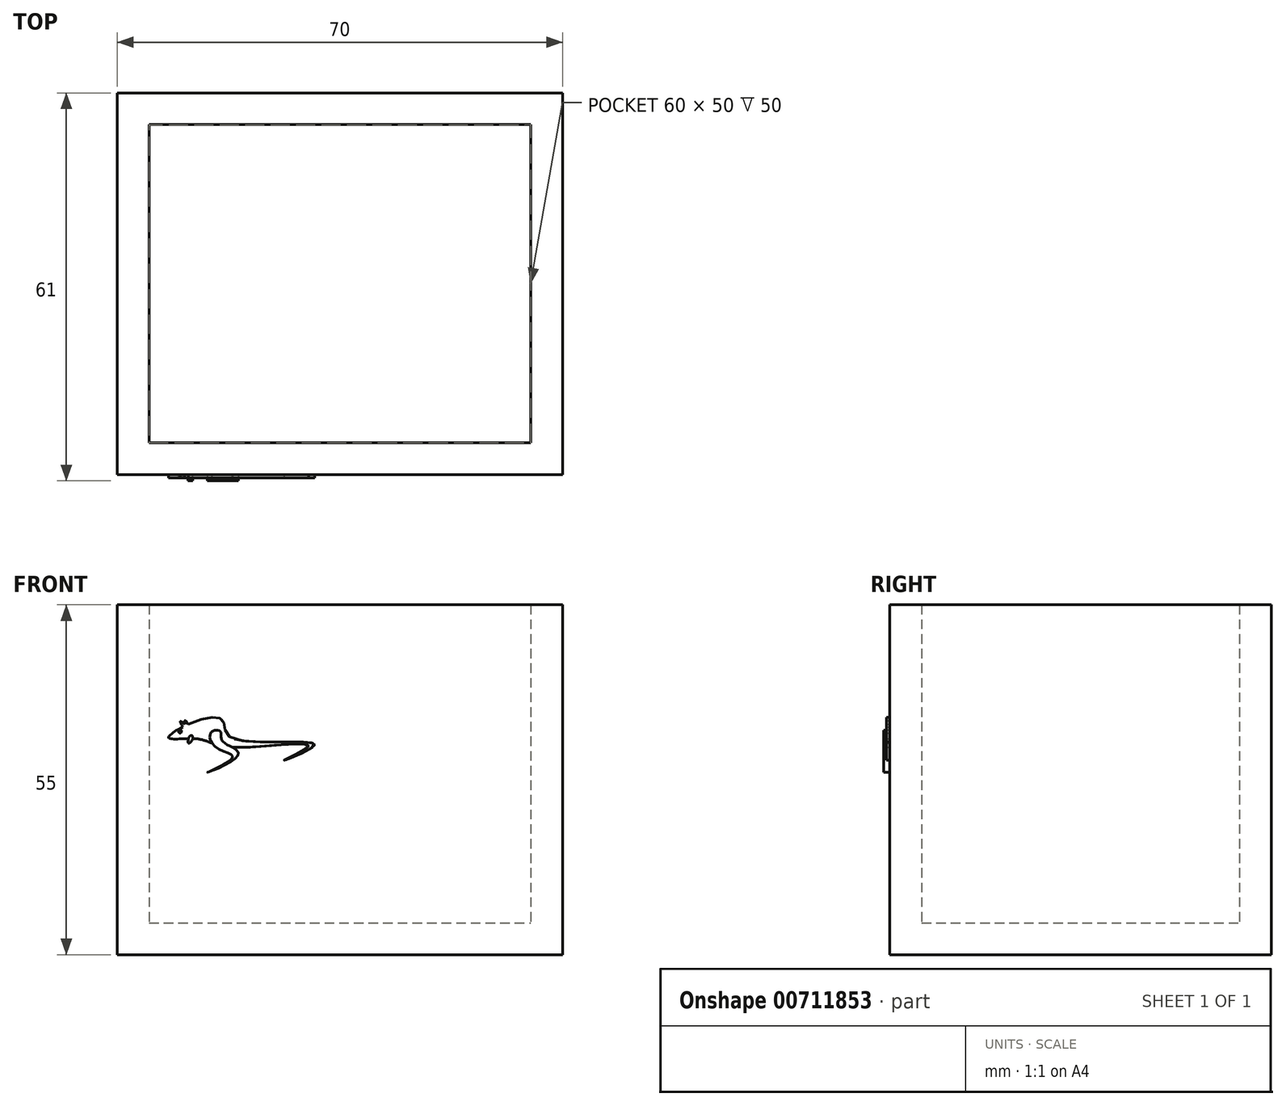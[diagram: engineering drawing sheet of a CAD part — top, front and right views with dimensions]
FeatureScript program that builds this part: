
annotation { "Feature Type Name" : "Feature", "Feature Type Description" : "" }
export const myFeature = defineFeature(function(context is Context, id is Id, definition is map)
    precondition{}
    {
        {
            var Q0;
            Q0=qCreatedBy(makeId("Top.planeOp"),FACE);
            var sketch = newSketch(context, id + "F0", { "sketchPlane" : qUnion([Q0])});
            skLineSegment(sketch, "E0.bottom", {"start": v(0, 0) * mm, "end": v(70, 0) * mm});
            skLineSegment(sketch, "E0.top", {"start": v(0, 60) * mm, "end": v(70, 60) * mm});
            skLineSegment(sketch, "E0.left", {"start": v(0, 0) * mm, "end": v(0, 60) * mm});
            skLineSegment(sketch, "E0.right", {"start": v(70, 0) * mm, "end": v(70, 60) * mm});
            skSolve(sketch);
        }
        {
            var Q0;
            Q0=makeQuery(id+"F0.imprint","IMPRINT",FACE,{"disambiguationData":[TD([[makeQuery(id+"F0.imprint","IMPRINT",EDGE,{"derivedFrom":sQuery(id+"F0.wireOp",EDGE,"E0.bottom")}),1.0]])]});
            extrude(context, id + "F1", {"entities" : qUnion([Q0]), "depth" : 5 * mm, "offsetDistance" : 25 * mm});
        }
        {
            var Q0;
            Q0=makeQuery(id+"F1.opExtrude","CAP_FACE",FACE,{"disambiguationData":[OSD([sQuery(id+"F0.wireOp",EDGE,"E0.bottom"),sQuery(id+"F0.wireOp",EDGE,"E0.top"),sQuery(id+"F0.wireOp",EDGE,"E0.left"),sQuery(id+"F0.wireOp",EDGE,"E0.right")])],"isStart":false});
            var sketch = newSketch(context, id + "F2", { "sketchPlane" : qUnion([Q0])});
            skLineSegment(sketch, "E1.bottom", {"start": v(0, 0) * mm, "end": v(5, 0) * mm});
            skLineSegment(sketch, "E1.top", {"start": v(0, 60) * mm, "end": v(5, 60) * mm});
            skLineSegment(sketch, "E1.left", {"start": v(0, 0) * mm, "end": v(0, 60) * mm});
            skLineSegment(sketch, "E1.right", {"start": v(5, 0) * mm, "end": v(5, 60) * mm});
            skLineSegment(sketch, "E2.bottom", {"start": v(70, 0) * mm, "end": v(65, 0) * mm});
            skLineSegment(sketch, "E2.top", {"start": v(70, 60) * mm, "end": v(65, 60) * mm});
            skLineSegment(sketch, "E2.left", {"start": v(70, 0) * mm, "end": v(70, 60) * mm});
            skLineSegment(sketch, "E2.right", {"start": v(65, 0) * mm, "end": v(65, 60) * mm});
            skLineSegment(sketch, "E3.bottom", {"start": v(5, 60) * mm, "end": v(65, 60) * mm});
            skLineSegment(sketch, "E3.top", {"start": v(5, 55) * mm, "end": v(65, 55) * mm});
            skLineSegment(sketch, "E3.left", {"start": v(5, 60) * mm, "end": v(5, 55) * mm});
            skLineSegment(sketch, "E3.right", {"start": v(65, 60) * mm, "end": v(65, 55) * mm});
            skLineSegment(sketch, "E4.bottom", {"start": v(5, 0) * mm, "end": v(65, 0) * mm});
            skLineSegment(sketch, "E4.top", {"start": v(5, 5) * mm, "end": v(65, 5) * mm});
            skLineSegment(sketch, "E4.left", {"start": v(5, 0) * mm, "end": v(5, 5) * mm});
            skLineSegment(sketch, "E4.right", {"start": v(65, 0) * mm, "end": v(65, 5) * mm});
            skSolve(sketch);
        }
        {
            var Q0;
            Q0=makeQuery(id+"F2.imprint","IMPRINT",FACE,{"disambiguationData":[TD([[makeQuery(id+"F2.imprint","IMPRINT",EDGE,{"derivedFrom":sQuery(id+"F2.wireOp",EDGE,"E1.bottom")}),1.0]])]});
            var Q1;
            Q1=makeQuery(id+"F2.imprint","IMPRINT",FACE,{"disambiguationData":[TD([[makeQuery(id+"F2.imprint","IMPRINT",EDGE,{"derivedFrom":sQuery(id+"F2.wireOp",EDGE,"E2.bottom")}),1.0]])]});
            var Q2;
            Q2=makeQuery(id+"F2.imprint","IMPRINT",FACE,{"disambiguationData":[TD([[makeQuery(id+"F2.imprint","IMPRINT",EDGE,{"derivedFrom":sQuery(id+"F2.wireOp",EDGE,"E4.bottom")}),1.0]])]});
            var Q3;
            Q3=makeQuery(id+"F2.imprint","IMPRINT",FACE,{"disambiguationData":[TD([[makeQuery(id+"F2.imprint","IMPRINT",EDGE,{"derivedFrom":sQuery(id+"F2.wireOp",EDGE,"E3.bottom")}),-1.0]])]});
            extrude(context, id + "F3", {"entities" : qUnion([Q0, Q1, Q2, Q3]), "operationType" : NewBodyOperationType.ADD, "depth" : 50 * mm, "offsetDistance" : 25 * mm});
        }
        {
            var Q0;
            Q0=makeQuery(id+"F3.boolean.opBoolean","MERGE",FACE,{"derivedFrom":[makeQuery(id+"F1.opExtrude","SWEPT_FACE",FACE,{"disambiguationData":[OSD([sQuery(id+"F0.wireOp",EDGE,"E0.bottom")])]}),makeQuery(id+"F3.opExtrude","SWEPT_FACE",FACE,{"disambiguationData":[OSD([sQuery(id+"F2.wireOp",EDGE,"E1.bottom"),sQuery(id+"F2.wireOp",EDGE,"E2.bottom"),sQuery(id+"F2.wireOp",EDGE,"E4.bottom")])]})]});
            var sketch = newSketch(context, id + "F4", { "sketchPlane" : qUnion([Q0])});
            skFitSpline(sketch, "E5", {"points": [v(8.08, 34.11) * mm, v(12.97, 36.93) * mm, v(16.63, 36.74) * mm, v(17.95, 34.11) * mm, v(31.01, 32.98) * mm, v(26.21, 30.57) * mm, v(30.07, 32.8) * mm, v(17.76, 32.6) * mm, v(12.6, 33.92) * mm, v(8.08, 34.11) * mm]});
            skFitSpline(sketch, "E6", {"points": [v(10.29, 35.8) * mm, v(9.93, 36.68) * mm, v(10.87, 36.1) * mm], "startDerivative": vector(-1.35, 2.53) * mm, "endDerivative": vector(2.48, -1.9) * mm});
            skFitSpline(sketch, "E7", {"points": [v(10.68, 36.25) * mm, v(10.62, 36.83) * mm, v(11.17, 36.23) * mm], "startDerivative": vector(-0.4, 1.81) * mm, "endDerivative": vector(1.33, -1.74) * mm});
            skFitSpline(sketch, "E8", {"points": [v(16.22, 35.08) * mm, v(16.5, 33.63) * mm, v(19.04, 31.47) * mm, v(14.18, 28.65) * mm, v(18.1, 30.95) * mm, v(15.5, 32.6) * mm, v(14.79, 35) * mm, v(16.22, 35.08) * mm]});
            skCircle(sketch, "E9", {"center": v(9.87, 35.1) * mm, "radius": 0.25 * mm});
            skFitSpline(sketch, "E10", {"points": [v(11.71, 34.47) * mm, v(11.81, 33.82) * mm, v(11.2, 33.24) * mm, v(11.15, 33.74) * mm, v(11.35, 34.3) * mm, v(11.71, 34.47) * mm]});
            skSolve(sketch);
        }
        {
            var Q0;
            {var subQ0=sQuery(id+"F4.wireOp",EDGE,"E8");var subQ1=makeQuery(id+"F4.imprint","INTERSECT",VERTEX,{"derivedFrom":[sQuery(id+"F4.wireOp",EDGE,"E5"),subQ0]});Q0=makeQuery(id+"F4.imprint","IMPRINT",FACE,{"disambiguationData":[TD([[makeQuery(id+"F4.imprint","IMPRINT",EDGE,{"disambiguationData":[TD([[subQ1,1.0]])],"derivedFrom":subQ0}),-1.0]])]});}
            var Q1;
            {var subQ0=sQuery(id+"F4.wireOp",EDGE,"E10");var subQ1=makeQuery(id+"F4.imprint","INTERSECT",VERTEX,{"derivedFrom":[sQuery(id+"F4.wireOp",EDGE,"E5"),subQ0]});Q1=makeQuery(id+"F4.imprint","IMPRINT",FACE,{"disambiguationData":[TD([[makeQuery(id+"F4.imprint","IMPRINT",EDGE,{"disambiguationData":[TD([[subQ1,-1.0]])],"derivedFrom":subQ0}),-1.0]])]});}
            extrude(context, id + "F5", {"entities" : qUnion([Q0, Q1]), "operationType" : NewBodyOperationType.ADD, "depth" : 1 * mm, "offsetDistance" : 25 * mm});
        }
        {
            var Q0;
            Q0 = qSketchRegion(id + "F4", true);
            extrude(context, id + "F6", {"entities" : qUnion([Q0]), "operationType" : NewBodyOperationType.ADD, "depth" : 0.5 * mm, "offsetDistance" : 25 * mm});
        }
    });
